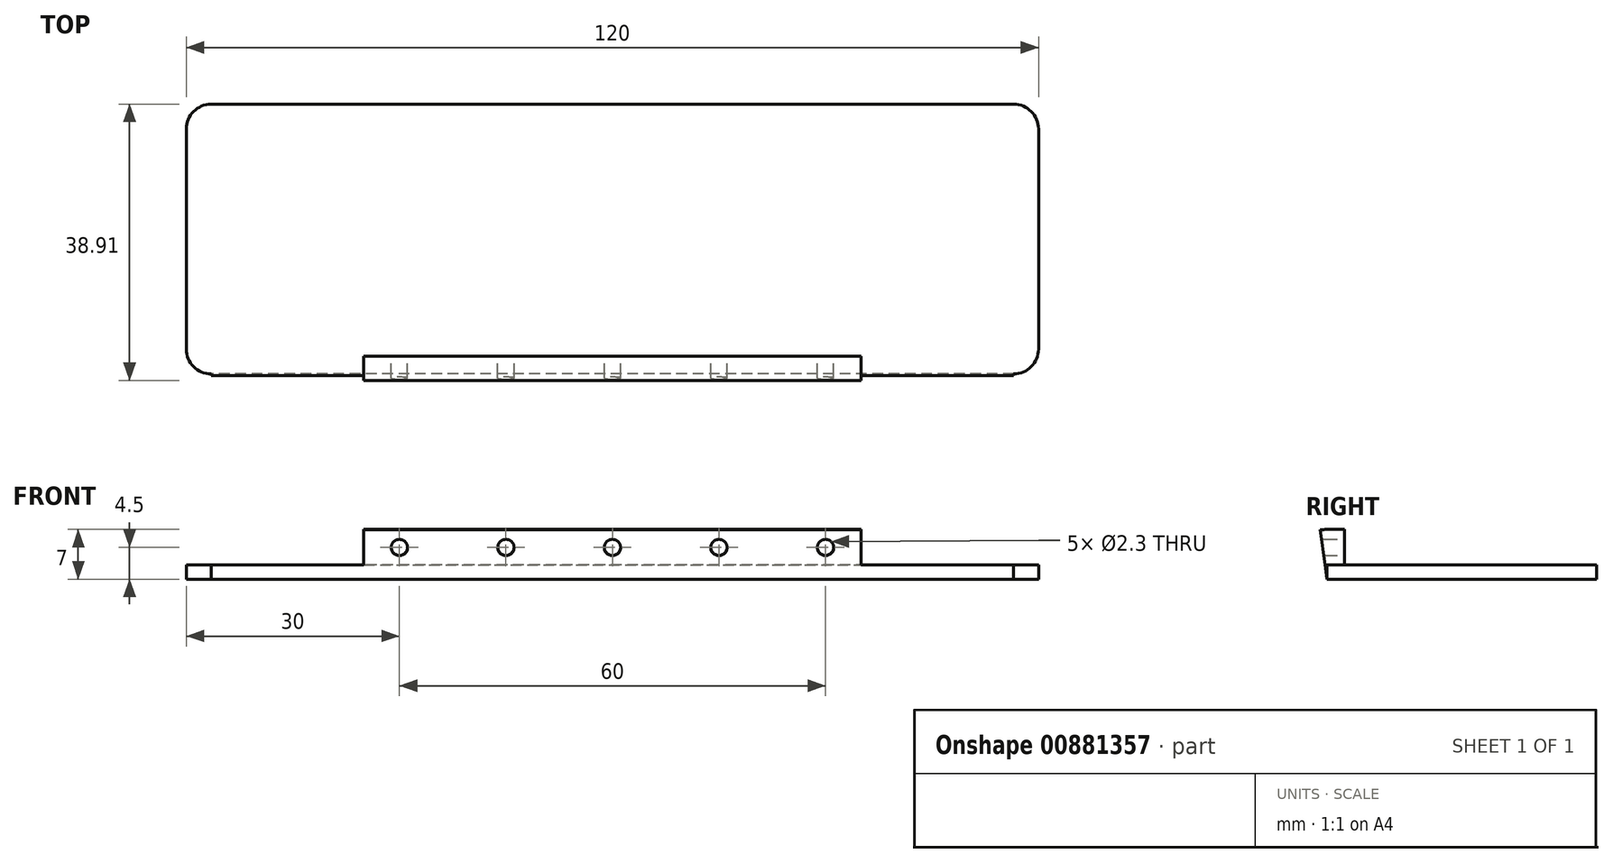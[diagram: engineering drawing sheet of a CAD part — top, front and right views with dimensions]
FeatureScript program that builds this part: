
annotation { "Feature Type Name" : "Feature", "Feature Type Description" : "" }
export const myFeature = defineFeature(function(context is Context, id is Id, definition is map)
    precondition{}
    {
        {
            var Q0;
            Q0=qCreatedBy(makeId("Top.planeOp"),FACE);
            var sketch = newSketch(context, id + "F0", { "sketchPlane" : qUnion([Q0])});
            skLineSegment(sketch, "E0.bottom", {"start": v(60, -19) * mm, "end": v(-60, -19) * mm});
            skLineSegment(sketch, "E0.top", {"start": v(60, 19) * mm, "end": v(-60, 19) * mm});
            skLineSegment(sketch, "E0.left", {"start": v(60, -19) * mm, "end": v(60, 19) * mm});
            skLineSegment(sketch, "E0.right", {"start": v(-60, -19) * mm, "end": v(-60, 19) * mm});
            skPoint(sketch, "E0.middle", {"position": v(0, 0) * mm});
            skSolve(sketch);
        }
        {
            var Q0;
            Q0=makeQuery(id+"F0.imprint","IMPRINT",FACE,{"disambiguationData":[TD([[makeQuery(id+"F0.imprint","IMPRINT",EDGE,{"derivedFrom":sQuery(id+"F0.wireOp",EDGE,"E0.bottom")}),-1.0]])]});
            extrude(context, id + "F1", {"entities" : qUnion([Q0]), "depth" : 2 * mm, "offsetDistance" : 25 * mm});
        }
        {
            var Q0;
            Q0=makeQuery(id+"F1.opExtrude","CAP_FACE",FACE,{"disambiguationData":[OSD([sQuery(id+"F0.wireOp",EDGE,"E0.bottom"),sQuery(id+"F0.wireOp",EDGE,"E0.top"),sQuery(id+"F0.wireOp",EDGE,"E0.left"),sQuery(id+"F0.wireOp",EDGE,"E0.right")])],"isStart":false});
            var sketch = newSketch(context, id + "F2", { "sketchPlane" : qUnion([Q0])});
            skPoint(sketch, "E1", {"position": v(0, -19) * mm});
            skPoint(sketch, "E2", {"position": v(-35, -19) * mm});
            skPoint(sketch, "E3", {"position": v(-35, -16.5) * mm});
            skPoint(sketch, "E4", {"position": v(35, -16.5) * mm});
            skPoint(sketch, "E5", {"position": v(35, -19) * mm});
            skLineSegment(sketch, "E6", {"start": v(-35, -19) * mm, "end": v(-35, -16.5) * mm});
            skLineSegment(sketch, "E7", {"start": v(-35, -16.5) * mm, "end": v(35, -16.5) * mm});
            skLineSegment(sketch, "E8", {"start": v(35, -16.5) * mm, "end": v(35, -19) * mm});
            skSolve(sketch);
        }
        {
            var Q0;
            {var subQ0=sQuery(id+"F2.wireOp",EDGE,"E6");Q0=makeQuery(id+"F2.imprint","IMPRINT",FACE,{"disambiguationData":[TD([[makeQuery(id+"F2.imprint","IMPRINT",EDGE,{"derivedFrom":subQ0}),-1.0]])]});}
            extrude(context, id + "F3", {"entities" : qUnion([Q0]), "operationType" : NewBodyOperationType.ADD, "depth" : 5 * mm, "offsetDistance" : 25 * mm});
        }
        {
            var Q0;
            {var subQ0=sQuery(id+"F0.wireOp",EDGE,"E0.bottom");Q0=makeQuery(id+"F3.boolean.opBoolean","MERGE",FACE,{"derivedFrom":[makeQuery(id+"F1.opExtrude","SWEPT_FACE",FACE,{"disambiguationData":[OSD([subQ0])]}),makeQuery(id+"F3.opExtrude","SWEPT_FACE",FACE,{"disambiguationData":[OSD([subQ0])]})]});}
            var sketch = newSketch(context, id + "F4", { "sketchPlane" : qUnion([Q0])});
            skPoint(sketch, "E9", {"position": v(0, 4.5) * mm});
            skPoint(sketch, "E9.positionSnap0", {"position": v(0, 0) * mm});
            skPoint(sketch, "E10", {"position": v(15, 4.5) * mm});
            skPoint(sketch, "E11", {"position": v(30, 4.5) * mm});
            skPoint(sketch, "E12", {"position": v(-15, 4.5) * mm});
            skPoint(sketch, "E13", {"position": v(-30, 4.5) * mm});
            skSolve(sketch);
        }
        {
            var Q0;
            Q0=sQuery(id+"F4.wireOp",VERTEX,"E13");
            var Q1;
            Q1=sQuery(id+"F4.wireOp",VERTEX,"E12");
            var Q2;
            Q2=sQuery(id+"F4.wireOp",VERTEX,"E9");
            var Q3;
            Q3=sQuery(id+"F4.wireOp",VERTEX,"E10");
            var Q4;
            Q4=sQuery(id+"F4.wireOp",VERTEX,"E11");
            var Q5;
            Q5=makeQuery(id+"F1.opExtrude","SWEPT_BODY",BODY,{"disambiguationData":[OSD([sQuery(id+"F0.wireOp",EDGE,"E0.bottom"),sQuery(id+"F0.wireOp",EDGE,"E0.top"),sQuery(id+"F0.wireOp",EDGE,"E0.left"),sQuery(id+"F0.wireOp",EDGE,"E0.right")])]});
            hole(context, id + "F5", {"style" : HoleStyle.SIMPLE, "endStyle" : HoleEndStyle.BLIND, "holeDiameter" : 2.3 * mm, "majorDiameter" : 5 * mm, "holeDepth" : 5 * mm, "isTappedThrough" : true, "tappedDepth" : 12 * mm, "tapClearance" : 3, "locations" : qUnion([Q0, Q1, Q2, Q3, Q4]), "scope" : qUnion([Q5]), "startStyle" : HoleStartStyle.SKETCH});
        }
        {
            var Q0;
            Q0=makeQuery(id+"F1.opExtrude","SWEPT_EDGE",EDGE,{"disambiguationData":[OSD([sQuery(id+"F0.wireOp",EDGE,"E0.bottom"),sQuery(id+"F0.wireOp",EDGE,"E0.right")])]});
            var Q1;
            Q1=makeQuery(id+"F1.opExtrude","SWEPT_EDGE",EDGE,{"disambiguationData":[OSD([sQuery(id+"F0.wireOp",EDGE,"E0.top"),sQuery(id+"F0.wireOp",EDGE,"E0.right")])]});
            var Q2;
            Q2=makeQuery(id+"F1.opExtrude","SWEPT_EDGE",EDGE,{"disambiguationData":[OSD([sQuery(id+"F0.wireOp",EDGE,"E0.top"),sQuery(id+"F0.wireOp",EDGE,"E0.left")])]});
            var Q3;
            Q3=makeQuery(id+"F1.opExtrude","SWEPT_EDGE",EDGE,{"disambiguationData":[OSD([sQuery(id+"F0.wireOp",EDGE,"E0.bottom"),sQuery(id+"F0.wireOp",EDGE,"E0.left")])]});
            fillet(context, id + "F6", {"entities" : qUnion([Q0, Q1, Q2, Q3]), "radius" : 3.5 * mm, "tangentPropagation" : true, "allowEdgeOverflow" : false});
        }
        {
            var Q0;
            {var subQ0=sQuery(id+"F0.wireOp",EDGE,"E0.bottom");Q0=makeQuery(id+"F3.boolean.opBoolean","MERGE",FACE,{"derivedFrom":[makeQuery(id+"F1.opExtrude","SWEPT_FACE",FACE,{"disambiguationData":[OSD([subQ0])]}),makeQuery(id+"F3.opExtrude","SWEPT_FACE",FACE,{"disambiguationData":[OSD([subQ0])]})]});}
            var Q1;
            Q1=makeQuery(id+"F1.opExtrude","CAP_EDGE",EDGE,{"disambiguationData":[OSD([sQuery(id+"F0.wireOp",EDGE,"E0.bottom")])],"isStart":true});
            revolve(context, id + "F7", {"operationType" : NewBodyOperationType.ADD, "surfaceOperationType" : NewSurfaceOperationType.NEW, "entities" : qUnion([Q0]), "axis" : qUnion([Q1]), "revolveType" : RevolveType.ONE_DIRECTION, "oppositeDirection" : true, "angle" : 7.5 * degree});
        }
    });
